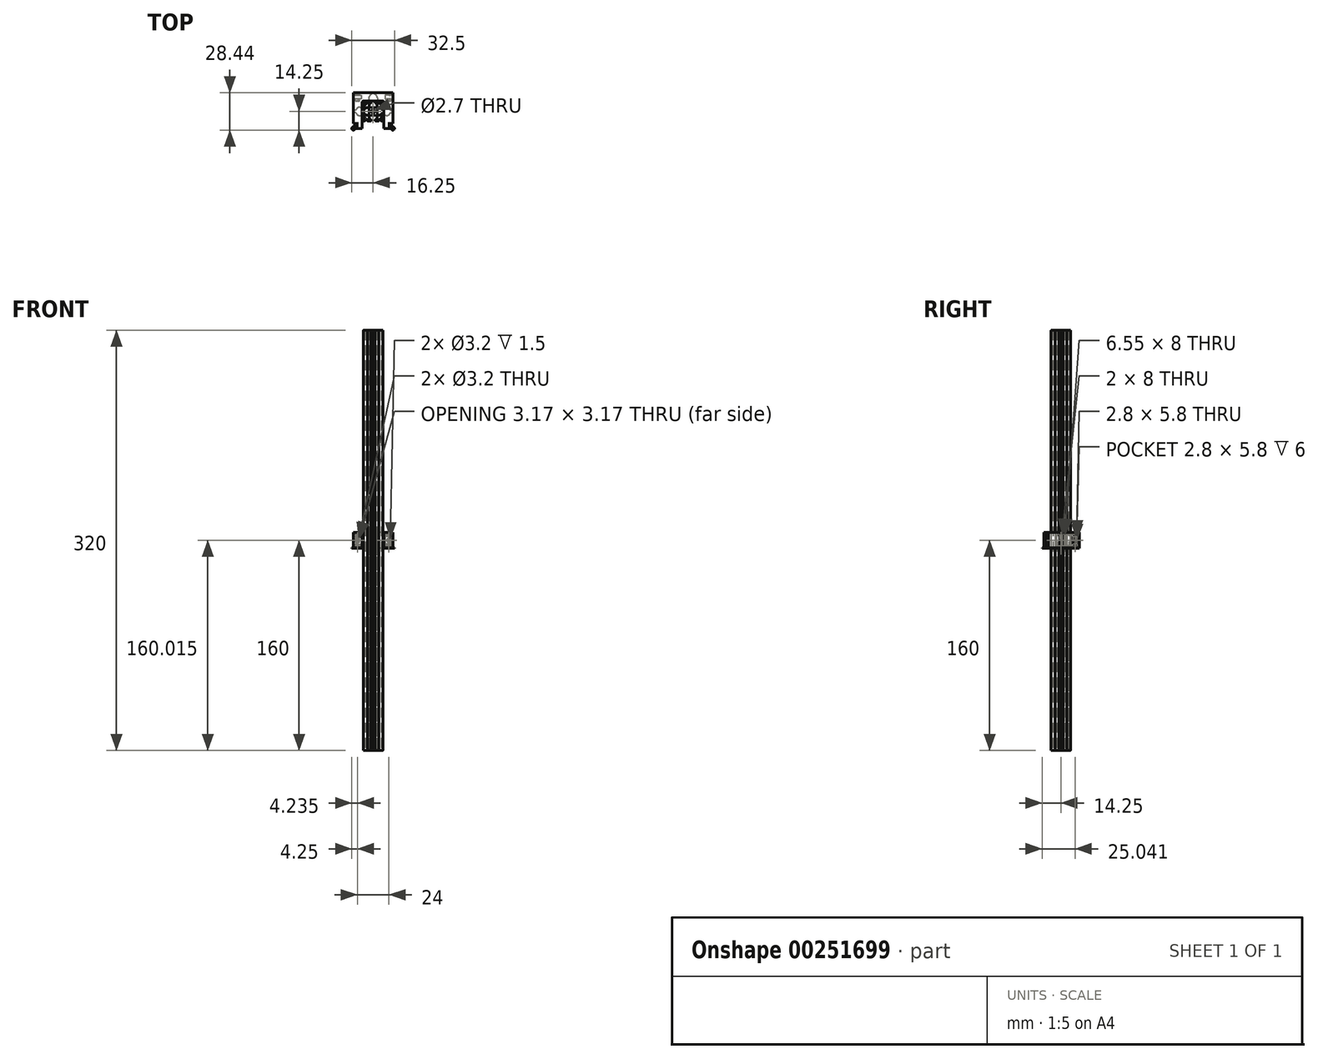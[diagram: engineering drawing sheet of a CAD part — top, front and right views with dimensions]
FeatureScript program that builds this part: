
annotation { "Feature Type Name" : "Feature", "Feature Type Description" : "" }
export const myFeature = defineFeature(function(context is Context, id is Id, definition is map)
    precondition{}
    {
        {
            var Q0;
            Q0=qCreatedBy(makeId("Top.planeOp"),FACE);
            var sketch = newSketch(context, id + "F0", { "sketchPlane" : qUnion([Q0])});
            skLineSegment(sketch, "E0", {"start": v(0, 0) * mm, "end": v(-7.5, -7.5) * mm, "construction": true});
            skArc(sketch, "E1", {"start": v(-1.35, 0) * mm, "mid": v(-1.25, -0.52) * mm, "end": v(-0.95, -0.95) * mm});
            skLineSegment(sketch, "E2", {"start": v(-7.5, -7) * mm, "end": v(-7.5, -6.72) * mm});
            skLineSegment(sketch, "E3", {"start": v(-7.35, -6.36) * mm, "end": v(-6.25, -5.26) * mm});
            skLineSegment(sketch, "E4", {"start": v(-6.6, -4.4) * mm, "end": v(-7, -4.4) * mm});
            skLineSegment(sketch, "E5", {"start": v(-7.5, -3.9) * mm, "end": v(-7.5, -2.1) * mm});
            skLineSegment(sketch, "E6", {"start": v(-7, -1.6) * mm, "end": v(-6.6, -1.6) * mm});
            skLineSegment(sketch, "E7", {"start": v(-6.1, -2.1) * mm, "end": v(-6.1, -2.7) * mm});
            skLineSegment(sketch, "E8", {"start": v(-5.9, -2.9) * mm, "end": v(-3.74, -2.9) * mm});
            skLineSegment(sketch, "E9", {"start": v(-3.25, -2.49) * mm, "end": v(-2.93, -0.73) * mm});
            skLineSegment(sketch, "E10", {"start": v(-2.73, -0.57) * mm, "end": v(-2.6, -0.57) * mm});
            skLineSegment(sketch, "E11", {"start": v(-2.4, -0.37) * mm, "end": v(-2.4, 0) * mm});
            skLineSegment(sketch, "E12", {"start": v(-2.4, 0) * mm, "end": v(-1.35, 0) * mm, "construction": true});
            skPoint(sketch, "E13.visualSharp", {"position": v(-5.4, -4.4) * mm});
            skArc(sketch, "E13.filletArc", {"start": v(-6.25, -5.26) * mm, "mid": v(-6.14, -4.71) * mm, "end": v(-6.6, -4.4) * mm});
            skPoint(sketch, "E14.visualSharp", {"position": v(-6.1, -2.9) * mm});
            skArc(sketch, "E14.filletArc", {"start": v(-6.1, -2.7) * mm, "mid": v(-6.04, -2.84) * mm, "end": v(-5.9, -2.9) * mm});
            skPoint(sketch, "E15.visualSharp", {"position": v(-6.1, -1.6) * mm});
            skArc(sketch, "E15.filletArc", {"start": v(-6.1, -2.1) * mm, "mid": v(-6.25, -1.75) * mm, "end": v(-6.6, -1.6) * mm});
            skPoint(sketch, "E16.visualSharp", {"position": v(-7.5, -1.6) * mm});
            skArc(sketch, "E16.filletArc", {"start": v(-7, -1.6) * mm, "mid": v(-7.35, -1.75) * mm, "end": v(-7.5, -2.1) * mm});
            skPoint(sketch, "E17.visualSharp", {"position": v(-7.5, -4.4) * mm});
            skArc(sketch, "E17.filletArc", {"start": v(-7.5, -3.9) * mm, "mid": v(-7.35, -4.26) * mm, "end": v(-7, -4.4) * mm});
            skPoint(sketch, "E18.visualSharp", {"position": v(-7.5, -6.51) * mm});
            skArc(sketch, "E18.filletArc", {"start": v(-7.35, -6.36) * mm, "mid": v(-7.46, -6.53) * mm, "end": v(-7.5, -6.72) * mm});
            skPoint(sketch, "E19.visualSharp", {"position": v(-3.32, -2.9) * mm});
            skArc(sketch, "E19.filletArc", {"start": v(-3.74, -2.9) * mm, "mid": v(-3.42, -2.78) * mm, "end": v(-3.25, -2.49) * mm});
            skPoint(sketch, "E20.visualSharp", {"position": v(-2.9, -0.57) * mm});
            skArc(sketch, "E20.filletArc", {"start": v(-2.73, -0.57) * mm, "mid": v(-2.86, -0.62) * mm, "end": v(-2.93, -0.73) * mm});
            skPoint(sketch, "E21.visualSharp", {"position": v(-2.4, -0.57) * mm});
            skArc(sketch, "E21.filletArc", {"start": v(-2.6, -0.57) * mm, "mid": v(-2.46, -0.51) * mm, "end": v(-2.4, -0.37) * mm});
            skLineSegment(sketch, "E22.0.MirrorCS", {"start": v(0, -2.4) * mm, "end": v(0, -1.35) * mm, "construction": true});
            skPoint(sketch, "E22.1.MirrorP", {"position": v(-4.4, -7.5) * mm});
            skArc(sketch, "E22.2.MirrorCS", {"start": v(-6.36, -7.35) * mm, "mid": v(-6.53, -7.46) * mm, "end": v(-6.72, -7.5) * mm});
            skPoint(sketch, "E22.3.MirrorP", {"position": v(-1.6, -7.5) * mm});
            skArc(sketch, "E22.4.MirrorCS", {"start": v(-1.6, -7) * mm, "mid": v(-1.75, -7.35) * mm, "end": v(-2.1, -7.5) * mm});
            skArc(sketch, "E22.5.MirrorCS", {"start": v(-0.57, -2.73) * mm, "mid": v(-0.62, -2.86) * mm, "end": v(-0.73, -2.93) * mm});
            skPoint(sketch, "E22.6.MirrorP", {"position": v(-1.6, -6.1) * mm});
            skLineSegment(sketch, "E22.7.MirrorCS", {"start": v(-3.9, -7.5) * mm, "end": v(-2.1, -7.5) * mm});
            skArc(sketch, "E22.8.MirrorCS", {"start": v(-5.26, -6.25) * mm, "mid": v(-4.71, -6.14) * mm, "end": v(-4.4, -6.6) * mm});
            skPoint(sketch, "E22.9.MirrorP", {"position": v(-0.57, -2.4) * mm});
            skPoint(sketch, "E22.10.MirrorP", {"position": v(-4.4, -5.4) * mm});
            skArc(sketch, "E22.11.MirrorCS", {"start": v(-2.7, -6.1) * mm, "mid": v(-2.84, -6.04) * mm, "end": v(-2.9, -5.9) * mm});
            skPoint(sketch, "E22.12.MirrorP", {"position": v(-0.57, -2.9) * mm});
            skLineSegment(sketch, "E22.13.MirrorCS", {"start": v(-7, -7.5) * mm, "end": v(-6.72, -7.5) * mm});
            skLineSegment(sketch, "E22.14.MirrorCS", {"start": v(-1.6, -7) * mm, "end": v(-1.6, -6.6) * mm});
            skLineSegment(sketch, "E22.15.MirrorCS", {"start": v(-6.36, -7.35) * mm, "end": v(-5.26, -6.25) * mm});
            skArc(sketch, "E22.16.MirrorCS", {"start": v(-2.1, -6.1) * mm, "mid": v(-1.75, -6.25) * mm, "end": v(-1.6, -6.6) * mm});
            skLineSegment(sketch, "E22.17.MirrorCS", {"start": v(-4.4, -6.6) * mm, "end": v(-4.4, -7) * mm});
            skArc(sketch, "E22.18.MirrorCS", {"start": v(-2.9, -3.74) * mm, "mid": v(-2.78, -3.42) * mm, "end": v(-2.49, -3.25) * mm});
            skLineSegment(sketch, "E22.19.MirrorCS", {"start": v(-2.9, -5.9) * mm, "end": v(-2.9, -3.74) * mm});
            skLineSegment(sketch, "E22.20.MirrorCS", {"start": v(-2.1, -6.1) * mm, "end": v(-2.7, -6.1) * mm});
            skArc(sketch, "E22.21.MirrorCS", {"start": v(-0.57, -2.6) * mm, "mid": v(-0.51, -2.46) * mm, "end": v(-0.37, -2.4) * mm});
            skLineSegment(sketch, "E22.22.MirrorCS", {"start": v(-0.37, -2.4) * mm, "end": v(0, -2.4) * mm});
            skPoint(sketch, "E22.23.MirrorP", {"position": v(-6.51, -7.5) * mm});
            skPoint(sketch, "E22.24.MirrorP", {"position": v(-2.9, -6.1) * mm});
            skLineSegment(sketch, "E22.25.MirrorCS", {"start": v(-2.49, -3.25) * mm, "end": v(-0.73, -2.93) * mm});
            skLineSegment(sketch, "E22.26.MirrorCS", {"start": v(-0.57, -2.73) * mm, "end": v(-0.57, -2.6) * mm});
            skArc(sketch, "E22.27.MirrorCS", {"start": v(0, -1.35) * mm, "mid": v(-0.52, -1.25) * mm, "end": v(-0.95, -0.95) * mm});
            skArc(sketch, "E22.28.MirrorCS", {"start": v(-3.9, -7.5) * mm, "mid": v(-4.26, -7.35) * mm, "end": v(-4.4, -7) * mm});
            skPoint(sketch, "E22.29.MirrorP", {"position": v(-2.9, -3.32) * mm});
            skPoint(sketch, "E23.visualSharp", {"position": v(-7.5, -7.5) * mm});
            skArc(sketch, "E23.filletArc", {"start": v(-7.5, -7) * mm, "mid": v(-7.35, -7.35) * mm, "end": v(-7, -7.5) * mm});
            skLineSegment(sketch, "E24.0.MirrorCS", {"start": v(0, 2.4) * mm, "end": v(0, 1.35) * mm, "construction": true});
            skLineSegment(sketch, "E24.1.MirrorCS", {"start": v(-2.1, 6.1) * mm, "end": v(-2.7, 6.1) * mm});
            skLineSegment(sketch, "E24.2.MirrorCS", {"start": v(-7.5, 3.9) * mm, "end": v(-7.5, 2.1) * mm});
            skLineSegment(sketch, "E24.3.MirrorCS", {"start": v(-7, 1.6) * mm, "end": v(-6.6, 1.6) * mm});
            skArc(sketch, "E24.4.MirrorCS", {"start": v(-6.1, 2.1) * mm, "mid": v(-6.25, 1.75) * mm, "end": v(-6.6, 1.6) * mm});
            skPoint(sketch, "E24.5.MirrorP", {"position": v(-3.32, 2.9) * mm});
            skPoint(sketch, "E24.6.MirrorP", {"position": v(-0.57, 2.9) * mm});
            skArc(sketch, "E24.7.MirrorCS", {"start": v(-0.57, 2.6) * mm, "mid": v(-0.51, 2.46) * mm, "end": v(-0.37, 2.4) * mm});
            skArc(sketch, "E24.8.MirrorCS", {"start": v(-2.6, 0.57) * mm, "mid": v(-2.46, 0.51) * mm, "end": v(-2.4, 0.37) * mm});
            skLineSegment(sketch, "E24.9.MirrorCS", {"start": v(-0.37, 2.4) * mm, "end": v(0, 2.4) * mm});
            skArc(sketch, "E24.10.MirrorCS", {"start": v(-6.1, 2.7) * mm, "mid": v(-6.04, 2.84) * mm, "end": v(-5.9, 2.9) * mm});
            skPoint(sketch, "E24.11.MirrorP", {"position": v(-4.4, 5.4) * mm});
            skLineSegment(sketch, "E24.12.MirrorCS", {"start": v(-2.9, 5.9) * mm, "end": v(-2.9, 3.74) * mm});
            skLineSegment(sketch, "E24.13.MirrorCS", {"start": v(-7.35, 6.36) * mm, "end": v(-6.25, 5.26) * mm});
            skPoint(sketch, "E24.14.MirrorP", {"position": v(-7.5, 6.51) * mm});
            skArc(sketch, "E24.15.MirrorCS", {"start": v(-3.74, 2.9) * mm, "mid": v(-3.42, 2.78) * mm, "end": v(-3.25, 2.49) * mm});
            skArc(sketch, "E24.16.MirrorCS", {"start": v(-2.1, 6.1) * mm, "mid": v(-1.75, 6.25) * mm, "end": v(-1.6, 6.6) * mm});
            skArc(sketch, "E24.17.MirrorCS", {"start": v(-7, 1.6) * mm, "mid": v(-7.35, 1.75) * mm, "end": v(-7.5, 2.1) * mm});
            skPoint(sketch, "E24.18.MirrorP", {"position": v(-1.6, 6.1) * mm});
            skPoint(sketch, "E24.19.MirrorP", {"position": v(-7.5, 4.4) * mm});
            skLineSegment(sketch, "E24.20.MirrorCS", {"start": v(-4.4, 6.6) * mm, "end": v(-4.4, 7) * mm});
            skArc(sketch, "E24.21.MirrorCS", {"start": v(-7.5, 3.9) * mm, "mid": v(-7.35, 4.26) * mm, "end": v(-7, 4.4) * mm});
            skPoint(sketch, "E24.22.MirrorP", {"position": v(-0.57, 2.4) * mm});
            skLineSegment(sketch, "E24.23.MirrorCS", {"start": v(-5.9, 2.9) * mm, "end": v(-3.74, 2.9) * mm});
            skArc(sketch, "E24.24.MirrorCS", {"start": v(-2.9, 3.74) * mm, "mid": v(-2.78, 3.42) * mm, "end": v(-2.49, 3.25) * mm});
            skArc(sketch, "E24.25.MirrorCS", {"start": v(-7.35, 6.36) * mm, "mid": v(-7.46, 6.53) * mm, "end": v(-7.5, 6.72) * mm});
            skPoint(sketch, "E24.26.MirrorP", {"position": v(-6.1, 2.9) * mm});
            skPoint(sketch, "E24.27.MirrorP", {"position": v(-4.4, 7.5) * mm});
            skArc(sketch, "E24.28.MirrorCS", {"start": v(-5.26, 6.25) * mm, "mid": v(-4.71, 6.14) * mm, "end": v(-4.4, 6.6) * mm});
            skArc(sketch, "E24.29.MirrorCS", {"start": v(-7.5, 7) * mm, "mid": v(-7.35, 7.35) * mm, "end": v(-7, 7.5) * mm});
            skPoint(sketch, "E24.30.MirrorP", {"position": v(-6.1, 1.6) * mm});
            skPoint(sketch, "E24.31.MirrorP", {"position": v(-2.9, 3.32) * mm});
            skPoint(sketch, "E24.32.MirrorP", {"position": v(-1.6, 7.5) * mm});
            skPoint(sketch, "E24.33.MirrorP", {"position": v(-2.9, 6.1) * mm});
            skLineSegment(sketch, "E24.34.MirrorCS", {"start": v(-3.9, 7.5) * mm, "end": v(-2.1, 7.5) * mm});
            skLineSegment(sketch, "E24.35.MirrorCS", {"start": v(-7, 7.5) * mm, "end": v(-6.72, 7.5) * mm});
            skArc(sketch, "E24.36.MirrorCS", {"start": v(-3.9, 7.5) * mm, "mid": v(-4.26, 7.35) * mm, "end": v(-4.4, 7) * mm});
            skPoint(sketch, "E24.37.MirrorP", {"position": v(-7.5, 7.5) * mm});
            skLineSegment(sketch, "E24.38.MirrorCS", {"start": v(-1.6, 7) * mm, "end": v(-1.6, 6.6) * mm});
            skLineSegment(sketch, "E24.39.MirrorCS", {"start": v(-6.36, 7.35) * mm, "end": v(-5.26, 6.25) * mm});
            skPoint(sketch, "E24.40.MirrorP", {"position": v(-7.5, 1.6) * mm});
            skArc(sketch, "E24.41.MirrorCS", {"start": v(-2.7, 6.1) * mm, "mid": v(-2.84, 6.04) * mm, "end": v(-2.9, 5.9) * mm});
            skArc(sketch, "E24.42.MirrorCS", {"start": v(-6.36, 7.35) * mm, "mid": v(-6.53, 7.46) * mm, "end": v(-6.72, 7.5) * mm});
            skLineSegment(sketch, "E24.43.MirrorCS", {"start": v(-2.49, 3.25) * mm, "end": v(-0.73, 2.93) * mm});
            skPoint(sketch, "E24.44.MirrorP", {"position": v(-2.9, 0.57) * mm});
            skLineSegment(sketch, "E24.45.MirrorCS", {"start": v(-6.6, 4.4) * mm, "end": v(-7, 4.4) * mm});
            skArc(sketch, "E24.46.MirrorCS", {"start": v(-1.6, 7) * mm, "mid": v(-1.75, 7.35) * mm, "end": v(-2.1, 7.5) * mm});
            skArc(sketch, "E24.47.MirrorCS", {"start": v(-2.73, 0.57) * mm, "mid": v(-2.86, 0.62) * mm, "end": v(-2.93, 0.73) * mm});
            skArc(sketch, "E24.48.MirrorCS", {"start": v(-6.25, 5.26) * mm, "mid": v(-6.14, 4.71) * mm, "end": v(-6.6, 4.4) * mm});
            skLineSegment(sketch, "E24.49.MirrorCS", {"start": v(-0.57, 2.73) * mm, "end": v(-0.57, 2.6) * mm});
            skLineSegment(sketch, "E24.50.MirrorCS", {"start": v(-2.73, 0.57) * mm, "end": v(-2.6, 0.57) * mm});
            skArc(sketch, "E24.51.MirrorCS", {"start": v(-1.35, 0) * mm, "mid": v(-1.25, 0.52) * mm, "end": v(-0.95, 0.95) * mm});
            skPoint(sketch, "E24.52.MirrorP", {"position": v(-2.4, 0.57) * mm});
            skPoint(sketch, "E24.53.MirrorP", {"position": v(-5.4, 4.4) * mm});
            skLineSegment(sketch, "E24.54.MirrorCS", {"start": v(-2.4, 0.37) * mm, "end": v(-2.4, 0) * mm});
            skArc(sketch, "E24.55.MirrorCS", {"start": v(0, 1.35) * mm, "mid": v(-0.52, 1.25) * mm, "end": v(-0.95, 0.95) * mm});
            skLineSegment(sketch, "E24.56.MirrorCS", {"start": v(-3.25, 2.49) * mm, "end": v(-2.93, 0.73) * mm});
            skLineSegment(sketch, "E24.57.MirrorCS", {"start": v(-6.1, 2.1) * mm, "end": v(-6.1, 2.7) * mm});
            skLineSegment(sketch, "E24.58.MirrorCS", {"start": v(-7.5, 7) * mm, "end": v(-7.5, 6.72) * mm});
            skArc(sketch, "E24.59.MirrorCS", {"start": v(-0.57, 2.73) * mm, "mid": v(-0.62, 2.86) * mm, "end": v(-0.73, 2.93) * mm});
            skPoint(sketch, "E24.60.MirrorP", {"position": v(-6.51, 7.5) * mm});
            skLineSegment(sketch, "E25.0.MirrorCS", {"start": v(7, -7.5) * mm, "end": v(6.72, -7.5) * mm});
            skLineSegment(sketch, "E25.1.MirrorCS", {"start": v(0.57, 2.73) * mm, "end": v(0.57, 2.6) * mm});
            skLineSegment(sketch, "E25.2.MirrorCS", {"start": v(0.37, 2.4) * mm, "end": v(0, 2.4) * mm});
            skLineSegment(sketch, "E25.3.MirrorCS", {"start": v(7, 7.5) * mm, "end": v(6.72, 7.5) * mm});
            skLineSegment(sketch, "E25.4.MirrorCS", {"start": v(1.6, -7) * mm, "end": v(1.6, -6.6) * mm});
            skLineSegment(sketch, "E25.5.MirrorCS", {"start": v(2.73, 0.57) * mm, "end": v(2.6, 0.57) * mm});
            skLineSegment(sketch, "E25.6.MirrorCS", {"start": v(7, 1.6) * mm, "end": v(6.6, 1.6) * mm});
            skLineSegment(sketch, "E25.7.MirrorCS", {"start": v(5.9, 2.9) * mm, "end": v(3.74, 2.9) * mm});
            skLineSegment(sketch, "E25.8.MirrorCS", {"start": v(7.35, 6.36) * mm, "end": v(6.25, 5.26) * mm});
            skArc(sketch, "E25.9.MirrorCS", {"start": v(2.7, -6.1) * mm, "mid": v(2.84, -6.04) * mm, "end": v(2.9, -5.9) * mm});
            skArc(sketch, "E25.10.MirrorCS", {"start": v(2.9, 3.74) * mm, "mid": v(2.78, 3.42) * mm, "end": v(2.49, 3.25) * mm});
            skPoint(sketch, "E25.11.MirrorP", {"position": v(1.6, -7.5) * mm});
            skPoint(sketch, "E25.12.MirrorP", {"position": v(6.1, -1.6) * mm});
            skPoint(sketch, "E25.13.MirrorP", {"position": v(2.9, 3.32) * mm});
            skPoint(sketch, "E25.14.MirrorP", {"position": v(7.5, -1.6) * mm});
            skArc(sketch, "E25.15.MirrorCS", {"start": v(1.6, 7) * mm, "mid": v(1.75, 7.35) * mm, "end": v(2.1, 7.5) * mm});
            skLineSegment(sketch, "E25.16.MirrorCS", {"start": v(6.1, -2.1) * mm, "end": v(6.1, -2.7) * mm});
            skLineSegment(sketch, "E25.17.MirrorCS", {"start": v(2.4, 0.37) * mm, "end": v(2.4, 0) * mm});
            skArc(sketch, "E25.18.MirrorCS", {"start": v(7, -1.6) * mm, "mid": v(7.35, -1.75) * mm, "end": v(7.5, -2.1) * mm});
            skArc(sketch, "E25.19.MirrorCS", {"start": v(7.5, 7) * mm, "mid": v(7.35, 7.35) * mm, "end": v(7, 7.5) * mm});
            skArc(sketch, "E25.20.MirrorCS", {"start": v(2.1, -6.1) * mm, "mid": v(1.75, -6.25) * mm, "end": v(1.6, -6.6) * mm});
            skArc(sketch, "E25.21.MirrorCS", {"start": v(6.1, 2.1) * mm, "mid": v(6.25, 1.75) * mm, "end": v(6.6, 1.6) * mm});
            skLineSegment(sketch, "E25.22.MirrorCS", {"start": v(4.4, 6.6) * mm, "end": v(4.4, 7) * mm});
            skLineSegment(sketch, "E25.23.MirrorCS", {"start": v(6.6, 4.4) * mm, "end": v(7, 4.4) * mm});
            skArc(sketch, "E25.24.MirrorCS", {"start": v(7, 1.6) * mm, "mid": v(7.35, 1.75) * mm, "end": v(7.5, 2.1) * mm});
            skArc(sketch, "E25.25.MirrorCS", {"start": v(0, -1.35) * mm, "mid": v(0.52, -1.25) * mm, "end": v(0.95, -0.95) * mm});
            skLineSegment(sketch, "E25.26.MirrorCS", {"start": v(3.9, -7.5) * mm, "end": v(2.1, -7.5) * mm});
            skLineSegment(sketch, "E25.27.MirrorCS", {"start": v(2.1, 6.1) * mm, "end": v(2.7, 6.1) * mm});
            skLineSegment(sketch, "E25.28.MirrorCS", {"start": v(2.73, -0.57) * mm, "end": v(2.6, -0.57) * mm});
            skLineSegment(sketch, "E25.29.MirrorCS", {"start": v(4.4, -6.6) * mm, "end": v(4.4, -7) * mm});
            skLineSegment(sketch, "E25.30.MirrorCS", {"start": v(3.9, 7.5) * mm, "end": v(2.1, 7.5) * mm});
            skArc(sketch, "E25.31.MirrorCS", {"start": v(0.57, -2.73) * mm, "mid": v(0.62, -2.86) * mm, "end": v(0.73, -2.93) * mm});
            skArc(sketch, "E25.32.MirrorCS", {"start": v(0.57, 2.6) * mm, "mid": v(0.51, 2.46) * mm, "end": v(0.37, 2.4) * mm});
            skPoint(sketch, "E25.33.MirrorP", {"position": v(6.51, -7.5) * mm});
            skArc(sketch, "E25.34.MirrorCS", {"start": v(3.9, -7.5) * mm, "mid": v(4.26, -7.35) * mm, "end": v(4.4, -7) * mm});
            skArc(sketch, "E25.35.MirrorCS", {"start": v(2.7, 6.1) * mm, "mid": v(2.84, 6.04) * mm, "end": v(2.9, 5.9) * mm});
            skPoint(sketch, "E25.36.MirrorP", {"position": v(0.57, -2.4) * mm});
            skPoint(sketch, "E25.37.MirrorP", {"position": v(0.57, 2.9) * mm});
            skLineSegment(sketch, "E25.38.MirrorCS", {"start": v(3.25, -2.49) * mm, "end": v(2.93, -0.73) * mm});
            skPoint(sketch, "E25.39.MirrorP", {"position": v(5.4, -4.4) * mm});
            skPoint(sketch, "E25.40.MirrorP", {"position": v(2.4, -0.57) * mm});
            skLineSegment(sketch, "E25.41.MirrorCS", {"start": v(7.5, -7) * mm, "end": v(7.5, -6.72) * mm});
            skArc(sketch, "E25.42.MirrorCS", {"start": v(7.35, 6.36) * mm, "mid": v(7.46, 6.53) * mm, "end": v(7.5, 6.72) * mm});
            skPoint(sketch, "E25.43.MirrorP", {"position": v(4.4, 7.5) * mm});
            skArc(sketch, "E25.44.MirrorCS", {"start": v(6.25, 5.26) * mm, "mid": v(6.14, 4.71) * mm, "end": v(6.6, 4.4) * mm});
            skPoint(sketch, "E25.45.MirrorP", {"position": v(6.1, -2.9) * mm});
            skPoint(sketch, "E25.46.MirrorP", {"position": v(4.4, -7.5) * mm});
            skArc(sketch, "E25.47.MirrorCS", {"start": v(6.1, 2.7) * mm, "mid": v(6.04, 2.84) * mm, "end": v(5.9, 2.9) * mm});
            skLineSegment(sketch, "E25.48.MirrorCS", {"start": v(2.1, -6.1) * mm, "end": v(2.7, -6.1) * mm});
            skArc(sketch, "E25.49.MirrorCS", {"start": v(2.73, -0.57) * mm, "mid": v(2.86, -0.62) * mm, "end": v(2.93, -0.73) * mm});
            skArc(sketch, "E25.50.MirrorCS", {"start": v(7.35, -6.36) * mm, "mid": v(7.46, -6.53) * mm, "end": v(7.5, -6.72) * mm});
            skLineSegment(sketch, "E25.51.MirrorCS", {"start": v(3.25, 2.49) * mm, "end": v(2.93, 0.73) * mm});
            skArc(sketch, "E25.52.MirrorCS", {"start": v(2.9, -3.74) * mm, "mid": v(2.78, -3.42) * mm, "end": v(2.49, -3.25) * mm});
            skArc(sketch, "E25.53.MirrorCS", {"start": v(2.6, 0.57) * mm, "mid": v(2.46, 0.51) * mm, "end": v(2.4, 0.37) * mm});
            skPoint(sketch, "E25.54.MirrorP", {"position": v(2.9, 0.57) * mm});
            skPoint(sketch, "E25.55.MirrorP", {"position": v(7.5, -6.51) * mm});
            skLineSegment(sketch, "E25.56.MirrorCS", {"start": v(2.49, 3.25) * mm, "end": v(0.73, 2.93) * mm});
            skArc(sketch, "E25.57.MirrorCS", {"start": v(1.6, -7) * mm, "mid": v(1.75, -7.35) * mm, "end": v(2.1, -7.5) * mm});
            skArc(sketch, "E25.58.MirrorCS", {"start": v(2.1, 6.1) * mm, "mid": v(1.75, 6.25) * mm, "end": v(1.6, 6.6) * mm});
            skLineSegment(sketch, "E25.59.MirrorCS", {"start": v(0.57, -2.73) * mm, "end": v(0.57, -2.6) * mm});
            skLineSegment(sketch, "E25.60.MirrorCS", {"start": v(2.4, -0.37) * mm, "end": v(2.4, 0) * mm});
            skArc(sketch, "E25.61.MirrorCS", {"start": v(7.5, -3.9) * mm, "mid": v(7.35, -4.26) * mm, "end": v(7, -4.4) * mm});
            skLineSegment(sketch, "E25.62.MirrorCS", {"start": v(5.9, -2.9) * mm, "end": v(3.74, -2.9) * mm});
            skLineSegment(sketch, "E25.63.MirrorCS", {"start": v(7.5, -3.9) * mm, "end": v(7.5, -2.1) * mm});
            skLineSegment(sketch, "E25.64.MirrorCS", {"start": v(7, -1.6) * mm, "end": v(6.6, -1.6) * mm});
            skArc(sketch, "E25.65.MirrorCS", {"start": v(1.35, 0) * mm, "mid": v(1.25, -0.52) * mm, "end": v(0.95, -0.95) * mm});
            skPoint(sketch, "E25.66.MirrorP", {"position": v(7.5, 1.6) * mm});
            skPoint(sketch, "E25.67.MirrorP", {"position": v(1.6, 6.1) * mm});
            skLineSegment(sketch, "E25.68.MirrorCS", {"start": v(6.36, -7.35) * mm, "end": v(5.26, -6.25) * mm});
            skPoint(sketch, "E25.69.MirrorP", {"position": v(2.4, 0.57) * mm});
            skPoint(sketch, "E25.70.MirrorP", {"position": v(6.1, 1.6) * mm});
            skPoint(sketch, "E25.71.MirrorP", {"position": v(3.32, -2.9) * mm});
            skPoint(sketch, "E25.72.MirrorP", {"position": v(0.57, -2.9) * mm});
            skPoint(sketch, "E25.73.MirrorP", {"position": v(7.5, 4.4) * mm});
            skArc(sketch, "E25.74.MirrorCS", {"start": v(5.26, -6.25) * mm, "mid": v(4.71, -6.14) * mm, "end": v(4.4, -6.6) * mm});
            skArc(sketch, "E25.75.MirrorCS", {"start": v(7.5, -7) * mm, "mid": v(7.35, -7.35) * mm, "end": v(7, -7.5) * mm});
            skLineSegment(sketch, "E25.76.MirrorCS", {"start": v(2.49, -3.25) * mm, "end": v(0.73, -2.93) * mm});
            skArc(sketch, "E25.77.MirrorCS", {"start": v(3.74, 2.9) * mm, "mid": v(3.42, 2.78) * mm, "end": v(3.25, 2.49) * mm});
            skArc(sketch, "E25.78.MirrorCS", {"start": v(6.36, -7.35) * mm, "mid": v(6.53, -7.46) * mm, "end": v(6.72, -7.5) * mm});
            skArc(sketch, "E25.79.MirrorCS", {"start": v(7.5, 3.9) * mm, "mid": v(7.35, 4.26) * mm, "end": v(7, 4.4) * mm});
            skArc(sketch, "E25.80.MirrorCS", {"start": v(2.73, 0.57) * mm, "mid": v(2.86, 0.62) * mm, "end": v(2.93, 0.73) * mm});
            skArc(sketch, "E25.81.MirrorCS", {"start": v(6.36, 7.35) * mm, "mid": v(6.53, 7.46) * mm, "end": v(6.72, 7.5) * mm});
            skPoint(sketch, "E25.82.MirrorP", {"position": v(4.4, -5.4) * mm});
            skPoint(sketch, "E25.83.MirrorP", {"position": v(6.51, 7.5) * mm});
            skPoint(sketch, "E25.84.MirrorP", {"position": v(2.9, -0.57) * mm});
            skLineSegment(sketch, "E25.85.MirrorCS", {"start": v(2.9, -5.9) * mm, "end": v(2.9, -3.74) * mm});
            skLineSegment(sketch, "E25.86.MirrorCS", {"start": v(6.1, 2.1) * mm, "end": v(6.1, 2.7) * mm});
            skLineSegment(sketch, "E25.87.MirrorCS", {"start": v(6.36, 7.35) * mm, "end": v(5.26, 6.25) * mm});
            skArc(sketch, "E25.88.MirrorCS", {"start": v(0.57, 2.73) * mm, "mid": v(0.62, 2.86) * mm, "end": v(0.73, 2.93) * mm});
            skArc(sketch, "E25.89.MirrorCS", {"start": v(0.57, -2.6) * mm, "mid": v(0.51, -2.46) * mm, "end": v(0.37, -2.4) * mm});
            skLineSegment(sketch, "E25.90.MirrorCS", {"start": v(2.9, 5.9) * mm, "end": v(2.9, 3.74) * mm});
            skArc(sketch, "E25.91.MirrorCS", {"start": v(0, 1.35) * mm, "mid": v(0.52, 1.25) * mm, "end": v(0.95, 0.95) * mm});
            skArc(sketch, "E25.92.MirrorCS", {"start": v(2.6, -0.57) * mm, "mid": v(2.46, -0.51) * mm, "end": v(2.4, -0.37) * mm});
            skPoint(sketch, "E25.93.MirrorP", {"position": v(4.4, 5.4) * mm});
            skPoint(sketch, "E25.94.MirrorP", {"position": v(2.9, -3.32) * mm});
            skPoint(sketch, "E25.95.MirrorP", {"position": v(2.9, 6.1) * mm});
            skPoint(sketch, "E25.96.MirrorP", {"position": v(5.4, 4.4) * mm});
            skPoint(sketch, "E25.97.MirrorP", {"position": v(3.32, 2.9) * mm});
            skArc(sketch, "E25.98.MirrorCS", {"start": v(3.74, -2.9) * mm, "mid": v(3.42, -2.78) * mm, "end": v(3.25, -2.49) * mm});
            skArc(sketch, "E25.99.MirrorCS", {"start": v(3.9, 7.5) * mm, "mid": v(4.26, 7.35) * mm, "end": v(4.4, 7) * mm});
            skPoint(sketch, "E25.100.MirrorP", {"position": v(7.5, -4.4) * mm});
            skPoint(sketch, "E25.101.MirrorP", {"position": v(6.1, 2.9) * mm});
            skArc(sketch, "E25.102.MirrorCS", {"start": v(1.35, 0) * mm, "mid": v(1.25, 0.52) * mm, "end": v(0.95, 0.95) * mm});
            skArc(sketch, "E25.103.MirrorCS", {"start": v(5.26, 6.25) * mm, "mid": v(4.71, 6.14) * mm, "end": v(4.4, 6.6) * mm});
            skPoint(sketch, "E25.104.MirrorP", {"position": v(7.5, 6.51) * mm});
            skPoint(sketch, "E25.105.MirrorP", {"position": v(2.9, -6.1) * mm});
            skArc(sketch, "E25.106.MirrorCS", {"start": v(6.25, -5.26) * mm, "mid": v(6.14, -4.71) * mm, "end": v(6.6, -4.4) * mm});
            skArc(sketch, "E25.107.MirrorCS", {"start": v(6.1, -2.1) * mm, "mid": v(6.25, -1.75) * mm, "end": v(6.6, -1.6) * mm});
            skPoint(sketch, "E25.108.MirrorP", {"position": v(1.6, 7.5) * mm});
            skPoint(sketch, "E25.109.MirrorP", {"position": v(7.5, 7.5) * mm});
            skLineSegment(sketch, "E25.110.MirrorCS", {"start": v(0.37, -2.4) * mm, "end": v(0, -2.4) * mm});
            skPoint(sketch, "E25.111.MirrorP", {"position": v(7.5, -7.5) * mm});
            skLineSegment(sketch, "E25.112.MirrorCS", {"start": v(7.5, 7) * mm, "end": v(7.5, 6.72) * mm});
            skArc(sketch, "E25.113.MirrorCS", {"start": v(6.1, -2.7) * mm, "mid": v(6.04, -2.84) * mm, "end": v(5.9, -2.9) * mm});
            skLineSegment(sketch, "E25.114.MirrorCS", {"start": v(1.6, 7) * mm, "end": v(1.6, 6.6) * mm});
            skPoint(sketch, "E25.115.MirrorP", {"position": v(1.6, -6.1) * mm});
            skLineSegment(sketch, "E25.116.MirrorCS", {"start": v(7.35, -6.36) * mm, "end": v(6.25, -5.26) * mm});
            skLineSegment(sketch, "E25.117.MirrorCS", {"start": v(7.5, 3.9) * mm, "end": v(7.5, 2.1) * mm});
            skPoint(sketch, "E25.118.MirrorP", {"position": v(0.57, 2.4) * mm});
            skLineSegment(sketch, "E25.119.MirrorCS", {"start": v(6.6, -4.4) * mm, "end": v(7, -4.4) * mm});
            skSolve(sketch);
        }
        {
            var Q0;
            Q0=qCreatedBy(makeId("Top.planeOp"),FACE);
            var sketch = newSketch(context, id + "F1", { "sketchPlane" : qUnion([Q0])});
            skLineSegment(sketch, "E26.0", {"start": v(6.36, -7.35) * mm, "end": v(5.26, -6.25) * mm, "construction": true});
            skLineSegment(sketch, "E26.1", {"start": v(-3.25, -2.49) * mm, "end": v(-2.93, -0.73) * mm, "construction": true});
            skArc(sketch, "E26.2", {"start": v(5.26, 6.25) * mm, "mid": v(4.71, 6.14) * mm, "end": v(4.4, 6.6) * mm, "construction": true});
            skLineSegment(sketch, "E26.3", {"start": v(7.5, -3.9) * mm, "end": v(7.5, -2.1) * mm, "construction": true});
            skArc(sketch, "E26.4", {"start": v(6.25, 5.26) * mm, "mid": v(6.14, 4.71) * mm, "end": v(6.6, 4.4) * mm, "construction": true});
            skLineSegment(sketch, "E26.5", {"start": v(-5.9, 2.9) * mm, "end": v(-3.74, 2.9) * mm, "construction": true});
            skLineSegment(sketch, "E26.6", {"start": v(-2.9, 5.9) * mm, "end": v(-2.9, 3.74) * mm, "construction": true});
            skArc(sketch, "E26.7", {"start": v(0, 1.35) * mm, "mid": v(-0.52, 1.25) * mm, "end": v(-0.95, 0.95) * mm, "construction": true});
            skLineSegment(sketch, "E26.8", {"start": v(2.9, 5.9) * mm, "end": v(2.9, 3.74) * mm, "construction": true});
            skLineSegment(sketch, "E26.9", {"start": v(-2.49, -3.25) * mm, "end": v(-0.73, -2.93) * mm, "construction": true});
            skLineSegment(sketch, "E26.10", {"start": v(-7.5, -3.9) * mm, "end": v(-7.5, -2.1) * mm, "construction": true});
            skLineSegment(sketch, "E26.11", {"start": v(3.25, 2.49) * mm, "end": v(2.93, 0.73) * mm, "construction": true});
            skLineSegment(sketch, "E26.12", {"start": v(2.49, -3.25) * mm, "end": v(0.73, -2.93) * mm, "construction": true});
            skLineSegment(sketch, "E26.13", {"start": v(-3.9, 7.5) * mm, "end": v(-2.1, 7.5) * mm, "construction": true});
            skLineSegment(sketch, "E26.14", {"start": v(5.9, 2.9) * mm, "end": v(3.74, 2.9) * mm, "construction": true});
            skLineSegment(sketch, "E26.15", {"start": v(3.9, 7.5) * mm, "end": v(2.1, 7.5) * mm, "construction": true});
            skLineSegment(sketch, "E26.16", {"start": v(-3.9, -7.5) * mm, "end": v(-2.1, -7.5) * mm, "construction": true});
            skLineSegment(sketch, "E26.17", {"start": v(6.36, 7.35) * mm, "end": v(5.26, 6.25) * mm, "construction": true});
            skLineSegment(sketch, "E26.18", {"start": v(-7.5, 3.9) * mm, "end": v(-7.5, 2.1) * mm, "construction": true});
            skLineSegment(sketch, "E26.19", {"start": v(-2.49, 3.25) * mm, "end": v(-0.73, 2.93) * mm, "construction": true});
            skArc(sketch, "E26.20", {"start": v(-6.25, -5.26) * mm, "mid": v(-6.14, -4.71) * mm, "end": v(-6.6, -4.4) * mm, "construction": true});
            skLineSegment(sketch, "E26.21", {"start": v(-7.35, 6.36) * mm, "end": v(-6.25, 5.26) * mm, "construction": true});
            skLineSegment(sketch, "E26.22", {"start": v(5.9, -2.9) * mm, "end": v(3.74, -2.9) * mm, "construction": true});
            skArc(sketch, "E26.23", {"start": v(0, -1.35) * mm, "mid": v(-0.52, -1.25) * mm, "end": v(-0.95, -0.95) * mm, "construction": true});
            skLineSegment(sketch, "E26.24", {"start": v(-3.25, 2.49) * mm, "end": v(-2.93, 0.73) * mm, "construction": true});
            skArc(sketch, "E26.25", {"start": v(0, 1.35) * mm, "mid": v(0.52, 1.25) * mm, "end": v(0.95, 0.95) * mm, "construction": true});
            skArc(sketch, "E26.26", {"start": v(5.26, -6.25) * mm, "mid": v(4.71, -6.14) * mm, "end": v(4.4, -6.6) * mm, "construction": true});
            skLineSegment(sketch, "E26.27", {"start": v(-6.36, 7.35) * mm, "end": v(-5.26, 6.25) * mm, "construction": true});
            skLineSegment(sketch, "E26.28", {"start": v(3.25, -2.49) * mm, "end": v(2.93, -0.73) * mm, "construction": true});
            skArc(sketch, "E26.29", {"start": v(6.25, -5.26) * mm, "mid": v(6.14, -4.71) * mm, "end": v(6.6, -4.4) * mm, "construction": true});
            skLineSegment(sketch, "E26.30", {"start": v(7.5, 3.9) * mm, "end": v(7.5, 2.1) * mm, "construction": true});
            skArc(sketch, "E26.31", {"start": v(1.35, 0) * mm, "mid": v(1.25, 0.52) * mm, "end": v(0.95, 0.95) * mm, "construction": true});
            skLineSegment(sketch, "E26.32", {"start": v(7.35, -6.36) * mm, "end": v(6.25, -5.26) * mm, "construction": true});
            skLineSegment(sketch, "E26.33", {"start": v(-6.36, -7.35) * mm, "end": v(-5.26, -6.25) * mm, "construction": true});
            skLineSegment(sketch, "E26.34", {"start": v(-7.35, -6.36) * mm, "end": v(-6.25, -5.26) * mm, "construction": true});
            skLineSegment(sketch, "E26.35", {"start": v(0, 0) * mm, "end": v(-7.5, -7.5) * mm, "construction": true});
            skLineSegment(sketch, "E26.36", {"start": v(-5.9, -2.9) * mm, "end": v(-3.74, -2.9) * mm, "construction": true});
            skArc(sketch, "E26.37", {"start": v(-5.26, -6.25) * mm, "mid": v(-4.71, -6.14) * mm, "end": v(-4.4, -6.6) * mm, "construction": true});
            skArc(sketch, "E26.38", {"start": v(-5.26, 6.25) * mm, "mid": v(-4.71, 6.14) * mm, "end": v(-4.4, 6.6) * mm, "construction": true});
            skLineSegment(sketch, "E26.39", {"start": v(2.49, 3.25) * mm, "end": v(0.73, 2.93) * mm, "construction": true});
            skLineSegment(sketch, "E26.40", {"start": v(7.35, 6.36) * mm, "end": v(6.25, 5.26) * mm, "construction": true});
            skLineSegment(sketch, "E26.41", {"start": v(2.9, -5.9) * mm, "end": v(2.9, -3.74) * mm, "construction": true});
            skLineSegment(sketch, "E26.42", {"start": v(-2.9, -5.9) * mm, "end": v(-2.9, -3.74) * mm, "construction": true});
            skLineSegment(sketch, "E26.43", {"start": v(3.9, -7.5) * mm, "end": v(2.1, -7.5) * mm, "construction": true});
            skArc(sketch, "E26.44", {"start": v(0, -1.35) * mm, "mid": v(0.52, -1.25) * mm, "end": v(0.95, -0.95) * mm, "construction": true});
            skArc(sketch, "E26.45", {"start": v(-6.25, 5.26) * mm, "mid": v(-6.14, 4.71) * mm, "end": v(-6.6, 4.4) * mm, "construction": true});
            skArc(sketch, "E26.46", {"start": v(-1.35, 0) * mm, "mid": v(-1.25, 0.52) * mm, "end": v(-0.95, 0.95) * mm, "construction": true});
            skLineSegment(sketch, "E26.47", {"start": v(-2.4, 0) * mm, "end": v(-1.35, 0) * mm, "construction": true});
            skLineSegment(sketch, "E26.48", {"start": v(0, -2.4) * mm, "end": v(0, -1.35) * mm, "construction": true});
            skLineSegment(sketch, "E26.49", {"start": v(0, 2.4) * mm, "end": v(0, 1.35) * mm, "construction": true});
            skArc(sketch, "E26.50", {"start": v(6.1, 2.1) * mm, "mid": v(6.25, 1.75) * mm, "end": v(6.6, 1.6) * mm, "construction": true});
            skLineSegment(sketch, "E26.51", {"start": v(6.6, -4.4) * mm, "end": v(7, -4.4) * mm, "construction": true});
            skLineSegment(sketch, "E26.52", {"start": v(-6.1, -2.1) * mm, "end": v(-6.1, -2.7) * mm, "construction": true});
            skArc(sketch, "E26.53", {"start": v(-7, -1.6) * mm, "mid": v(-7.35, -1.75) * mm, "end": v(-7.5, -2.1) * mm, "construction": true});
            skArc(sketch, "E26.54", {"start": v(-1.6, -7) * mm, "mid": v(-1.75, -7.35) * mm, "end": v(-2.1, -7.5) * mm, "construction": true});
            skLineSegment(sketch, "E26.55", {"start": v(7, -1.6) * mm, "end": v(6.6, -1.6) * mm, "construction": true});
            skArc(sketch, "E26.56", {"start": v(3.74, -2.9) * mm, "mid": v(3.42, -2.78) * mm, "end": v(3.25, -2.49) * mm, "construction": true});
            skArc(sketch, "E26.57", {"start": v(-3.74, 2.9) * mm, "mid": v(-3.42, 2.78) * mm, "end": v(-3.25, 2.49) * mm, "construction": true});
            skArc(sketch, "E26.58", {"start": v(1.6, -7) * mm, "mid": v(1.75, -7.35) * mm, "end": v(2.1, -7.5) * mm, "construction": true});
            skArc(sketch, "E26.59", {"start": v(1.6, 7) * mm, "mid": v(1.75, 7.35) * mm, "end": v(2.1, 7.5) * mm, "construction": true});
            skLineSegment(sketch, "E26.60", {"start": v(1.6, -7) * mm, "end": v(1.6, -6.6) * mm, "construction": true});
            skArc(sketch, "E26.61", {"start": v(-3.9, 7.5) * mm, "mid": v(-4.26, 7.35) * mm, "end": v(-4.4, 7) * mm, "construction": true});
            skArc(sketch, "E26.62", {"start": v(7, -1.6) * mm, "mid": v(7.35, -1.75) * mm, "end": v(7.5, -2.1) * mm, "construction": true});
            skArc(sketch, "E26.63", {"start": v(-6.1, 2.1) * mm, "mid": v(-6.25, 1.75) * mm, "end": v(-6.6, 1.6) * mm, "construction": true});
            skArc(sketch, "E26.64", {"start": v(-7.5, -3.9) * mm, "mid": v(-7.35, -4.26) * mm, "end": v(-7, -4.4) * mm, "construction": true});
            skArc(sketch, "E26.65", {"start": v(7.5, -3.9) * mm, "mid": v(7.35, -4.26) * mm, "end": v(7, -4.4) * mm, "construction": true});
            skArc(sketch, "E26.66", {"start": v(-3.9, -7.5) * mm, "mid": v(-4.26, -7.35) * mm, "end": v(-4.4, -7) * mm, "construction": true});
            skArc(sketch, "E26.67", {"start": v(-1.35, 0) * mm, "mid": v(-1.25, -0.52) * mm, "end": v(-0.95, -0.95) * mm, "construction": true});
            skLineSegment(sketch, "E26.68", {"start": v(-6.1, 2.1) * mm, "end": v(-6.1, 2.7) * mm, "construction": true});
            skArc(sketch, "E26.69", {"start": v(-3.74, -2.9) * mm, "mid": v(-3.42, -2.78) * mm, "end": v(-3.25, -2.49) * mm, "construction": true});
            skArc(sketch, "E26.70", {"start": v(1.35, 0) * mm, "mid": v(1.25, -0.52) * mm, "end": v(0.95, -0.95) * mm, "construction": true});
            skArc(sketch, "E26.71", {"start": v(-2.9, -3.74) * mm, "mid": v(-2.78, -3.42) * mm, "end": v(-2.49, -3.25) * mm, "construction": true});
            skArc(sketch, "E26.72", {"start": v(-6.1, -2.1) * mm, "mid": v(-6.25, -1.75) * mm, "end": v(-6.6, -1.6) * mm, "construction": true});
            skArc(sketch, "E26.73", {"start": v(2.1, -6.1) * mm, "mid": v(1.75, -6.25) * mm, "end": v(1.6, -6.6) * mm, "construction": true});
            skArc(sketch, "E26.74", {"start": v(7, 1.6) * mm, "mid": v(7.35, 1.75) * mm, "end": v(7.5, 2.1) * mm, "construction": true});
            skLineSegment(sketch, "E26.75", {"start": v(4.4, 6.6) * mm, "end": v(4.4, 7) * mm, "construction": true});
            skArc(sketch, "E26.76", {"start": v(-7.5, 3.9) * mm, "mid": v(-7.35, 4.26) * mm, "end": v(-7, 4.4) * mm, "construction": true});
            skArc(sketch, "E26.77", {"start": v(-2.9, 3.74) * mm, "mid": v(-2.78, 3.42) * mm, "end": v(-2.49, 3.25) * mm, "construction": true});
            skArc(sketch, "E26.78", {"start": v(3.9, -7.5) * mm, "mid": v(4.26, -7.35) * mm, "end": v(4.4, -7) * mm, "construction": true});
            skLineSegment(sketch, "E26.79", {"start": v(1.6, 7) * mm, "end": v(1.6, 6.6) * mm, "construction": true});
            skLineSegment(sketch, "E26.80", {"start": v(4.4, -6.6) * mm, "end": v(4.4, -7) * mm, "construction": true});
            skArc(sketch, "E26.81", {"start": v(-2.1, 6.1) * mm, "mid": v(-1.75, 6.25) * mm, "end": v(-1.6, 6.6) * mm, "construction": true});
            skArc(sketch, "E26.82", {"start": v(2.9, -3.74) * mm, "mid": v(2.78, -3.42) * mm, "end": v(2.49, -3.25) * mm, "construction": true});
            skLineSegment(sketch, "E26.83", {"start": v(-4.4, -6.6) * mm, "end": v(-4.4, -7) * mm, "construction": true});
            skArc(sketch, "E26.84", {"start": v(-1.6, 7) * mm, "mid": v(-1.75, 7.35) * mm, "end": v(-2.1, 7.5) * mm, "construction": true});
            skLineSegment(sketch, "E26.85", {"start": v(-6.6, -4.4) * mm, "end": v(-7, -4.4) * mm, "construction": true});
            skLineSegment(sketch, "E26.86", {"start": v(-4.4, 6.6) * mm, "end": v(-4.4, 7) * mm, "construction": true});
            skLineSegment(sketch, "E26.87", {"start": v(6.1, 2.1) * mm, "end": v(6.1, 2.7) * mm, "construction": true});
            skArc(sketch, "E26.88", {"start": v(7.5, 3.9) * mm, "mid": v(7.35, 4.26) * mm, "end": v(7, 4.4) * mm, "construction": true});
            skArc(sketch, "E26.89", {"start": v(2.9, 3.74) * mm, "mid": v(2.78, 3.42) * mm, "end": v(2.49, 3.25) * mm, "construction": true});
            skArc(sketch, "E26.90", {"start": v(3.9, 7.5) * mm, "mid": v(4.26, 7.35) * mm, "end": v(4.4, 7) * mm, "construction": true});
            skArc(sketch, "E26.91", {"start": v(3.74, 2.9) * mm, "mid": v(3.42, 2.78) * mm, "end": v(3.25, 2.49) * mm, "construction": true});
            skArc(sketch, "E26.92", {"start": v(6.1, -2.1) * mm, "mid": v(6.25, -1.75) * mm, "end": v(6.6, -1.6) * mm, "construction": true});
            skLineSegment(sketch, "E26.93", {"start": v(6.6, 4.4) * mm, "end": v(7, 4.4) * mm, "construction": true});
            skArc(sketch, "E26.94", {"start": v(-7, 1.6) * mm, "mid": v(-7.35, 1.75) * mm, "end": v(-7.5, 2.1) * mm, "construction": true});
            skLineSegment(sketch, "E26.95", {"start": v(6.1, -2.1) * mm, "end": v(6.1, -2.7) * mm, "construction": true});
            skArc(sketch, "E26.96", {"start": v(-6.36, -7.35) * mm, "mid": v(-6.53, -7.46) * mm, "end": v(-6.72, -7.5) * mm, "construction": true});
            skArc(sketch, "E26.97", {"start": v(7.35, 6.36) * mm, "mid": v(7.46, 6.53) * mm, "end": v(7.5, 6.72) * mm, "construction": true});
            skLineSegment(sketch, "E26.98", {"start": v(7, 7.5) * mm, "end": v(6.72, 7.5) * mm, "construction": true});
            skArc(sketch, "E26.99", {"start": v(-7.35, -6.36) * mm, "mid": v(-7.46, -6.53) * mm, "end": v(-7.5, -6.72) * mm, "construction": true});
            skLineSegment(sketch, "E26.100", {"start": v(7, 1.6) * mm, "end": v(6.6, 1.6) * mm, "construction": true});
            skArc(sketch, "E26.101", {"start": v(7.5, 7) * mm, "mid": v(7.35, 7.35) * mm, "end": v(7, 7.5) * mm, "construction": true});
            skArc(sketch, "E26.102", {"start": v(2.1, 6.1) * mm, "mid": v(1.75, 6.25) * mm, "end": v(1.6, 6.6) * mm, "construction": true});
            skArc(sketch, "E26.103", {"start": v(0.57, -2.6) * mm, "mid": v(0.51, -2.46) * mm, "end": v(0.37, -2.4) * mm, "construction": true});
            skLineSegment(sketch, "E26.104", {"start": v(2.1, -6.1) * mm, "end": v(2.7, -6.1) * mm, "construction": true});
            skLineSegment(sketch, "E26.105", {"start": v(2.1, 6.1) * mm, "end": v(2.7, 6.1) * mm, "construction": true});
            skLineSegment(sketch, "E26.106", {"start": v(-7, 7.5) * mm, "end": v(-6.72, 7.5) * mm, "construction": true});
            skLineSegment(sketch, "E26.107", {"start": v(0.57, 2.73) * mm, "end": v(0.57, 2.6) * mm, "construction": true});
            skLineSegment(sketch, "E26.108", {"start": v(-7, -1.6) * mm, "end": v(-6.6, -1.6) * mm, "construction": true});
            skLineSegment(sketch, "E26.109", {"start": v(-2.1, 6.1) * mm, "end": v(-2.7, 6.1) * mm, "construction": true});
            skArc(sketch, "E26.110", {"start": v(-2.7, 6.1) * mm, "mid": v(-2.84, 6.04) * mm, "end": v(-2.9, 5.9) * mm, "construction": true});
            skLineSegment(sketch, "E26.111", {"start": v(-7.5, -7) * mm, "end": v(-7.5, -6.72) * mm, "construction": true});
            skArc(sketch, "E26.112", {"start": v(-7.5, -7) * mm, "mid": v(-7.35, -7.35) * mm, "end": v(-7, -7.5) * mm, "construction": true});
            skLineSegment(sketch, "E26.113", {"start": v(-6.6, 4.4) * mm, "end": v(-7, 4.4) * mm, "construction": true});
            skArc(sketch, "E26.114", {"start": v(6.36, 7.35) * mm, "mid": v(6.53, 7.46) * mm, "end": v(6.72, 7.5) * mm, "construction": true});
            skArc(sketch, "E26.115", {"start": v(-6.36, 7.35) * mm, "mid": v(-6.53, 7.46) * mm, "end": v(-6.72, 7.5) * mm, "construction": true});
            skArc(sketch, "E26.116", {"start": v(-2.1, -6.1) * mm, "mid": v(-1.75, -6.25) * mm, "end": v(-1.6, -6.6) * mm, "construction": true});
            skArc(sketch, "E26.117", {"start": v(0.57, -2.73) * mm, "mid": v(0.62, -2.86) * mm, "end": v(0.73, -2.93) * mm, "construction": true});
            skArc(sketch, "E26.118", {"start": v(6.1, -2.7) * mm, "mid": v(6.04, -2.84) * mm, "end": v(5.9, -2.9) * mm, "construction": true});
            skArc(sketch, "E26.119", {"start": v(0.57, 2.73) * mm, "mid": v(0.62, 2.86) * mm, "end": v(0.73, 2.93) * mm, "construction": true});
            skArc(sketch, "E26.120", {"start": v(0.57, 2.6) * mm, "mid": v(0.51, 2.46) * mm, "end": v(0.37, 2.4) * mm, "construction": true});
            skArc(sketch, "E26.121", {"start": v(6.1, 2.7) * mm, "mid": v(6.04, 2.84) * mm, "end": v(5.9, 2.9) * mm, "construction": true});
            skLineSegment(sketch, "E26.122", {"start": v(-7, 1.6) * mm, "end": v(-6.6, 1.6) * mm, "construction": true});
            skArc(sketch, "E26.123", {"start": v(-7.5, 7) * mm, "mid": v(-7.35, 7.35) * mm, "end": v(-7, 7.5) * mm, "construction": true});
            skArc(sketch, "E26.124", {"start": v(-2.7, -6.1) * mm, "mid": v(-2.84, -6.04) * mm, "end": v(-2.9, -5.9) * mm, "construction": true});
            skLineSegment(sketch, "E26.125", {"start": v(-2.1, -6.1) * mm, "end": v(-2.7, -6.1) * mm, "construction": true});
            skLineSegment(sketch, "E26.126", {"start": v(-1.6, 7) * mm, "end": v(-1.6, 6.6) * mm, "construction": true});
            skArc(sketch, "E26.127", {"start": v(-6.1, -2.7) * mm, "mid": v(-6.04, -2.84) * mm, "end": v(-5.9, -2.9) * mm, "construction": true});
            skLineSegment(sketch, "E26.128", {"start": v(-1.6, -7) * mm, "end": v(-1.6, -6.6) * mm, "construction": true});
            skArc(sketch, "E26.129", {"start": v(2.7, -6.1) * mm, "mid": v(2.84, -6.04) * mm, "end": v(2.9, -5.9) * mm, "construction": true});
            skLineSegment(sketch, "E26.130", {"start": v(2.4, -0.37) * mm, "end": v(2.4, 0) * mm, "construction": true});
            skArc(sketch, "E26.131", {"start": v(7.5, -7) * mm, "mid": v(7.35, -7.35) * mm, "end": v(7, -7.5) * mm, "construction": true});
            skArc(sketch, "E26.132", {"start": v(2.7, 6.1) * mm, "mid": v(2.84, 6.04) * mm, "end": v(2.9, 5.9) * mm, "construction": true});
            skArc(sketch, "E26.133", {"start": v(-6.1, 2.7) * mm, "mid": v(-6.04, 2.84) * mm, "end": v(-5.9, 2.9) * mm, "construction": true});
            skArc(sketch, "E26.134", {"start": v(7.35, -6.36) * mm, "mid": v(7.46, -6.53) * mm, "end": v(7.5, -6.72) * mm, "construction": true});
            skLineSegment(sketch, "E26.135", {"start": v(-7.5, 7) * mm, "end": v(-7.5, 6.72) * mm, "construction": true});
            skLineSegment(sketch, "E26.136", {"start": v(0.37, 2.4) * mm, "end": v(0, 2.4) * mm, "construction": true});
            skArc(sketch, "E26.137", {"start": v(-0.57, 2.73) * mm, "mid": v(-0.62, 2.86) * mm, "end": v(-0.73, 2.93) * mm, "construction": true});
            skArc(sketch, "E26.138", {"start": v(-0.57, -2.6) * mm, "mid": v(-0.51, -2.46) * mm, "end": v(-0.37, -2.4) * mm, "construction": true});
            skLineSegment(sketch, "E26.139", {"start": v(-2.4, -0.37) * mm, "end": v(-2.4, 0) * mm, "construction": true});
            skLineSegment(sketch, "E26.140", {"start": v(7.5, 7) * mm, "end": v(7.5, 6.72) * mm, "construction": true});
            skLineSegment(sketch, "E26.141", {"start": v(-7, -7.5) * mm, "end": v(-6.72, -7.5) * mm, "construction": true});
            skLineSegment(sketch, "E26.142", {"start": v(2.4, 0.37) * mm, "end": v(2.4, 0) * mm, "construction": true});
            skLineSegment(sketch, "E26.143", {"start": v(7.5, -7) * mm, "end": v(7.5, -6.72) * mm, "construction": true});
            skArc(sketch, "E26.144", {"start": v(-7.35, 6.36) * mm, "mid": v(-7.46, 6.53) * mm, "end": v(-7.5, 6.72) * mm, "construction": true});
            skLineSegment(sketch, "E26.145", {"start": v(0.37, -2.4) * mm, "end": v(0, -2.4) * mm, "construction": true});
            skLineSegment(sketch, "E26.146", {"start": v(7, -7.5) * mm, "end": v(6.72, -7.5) * mm, "construction": true});
            skArc(sketch, "E26.147", {"start": v(-0.57, 2.6) * mm, "mid": v(-0.51, 2.46) * mm, "end": v(-0.37, 2.4) * mm, "construction": true});
            skLineSegment(sketch, "E26.148", {"start": v(0.57, -2.73) * mm, "end": v(0.57, -2.6) * mm, "construction": true});
            skArc(sketch, "E26.149", {"start": v(6.36, -7.35) * mm, "mid": v(6.53, -7.46) * mm, "end": v(6.72, -7.5) * mm, "construction": true});
            skArc(sketch, "E26.150", {"start": v(-0.57, -2.73) * mm, "mid": v(-0.62, -2.86) * mm, "end": v(-0.73, -2.93) * mm, "construction": true});
            skLineSegment(sketch, "E26.151", {"start": v(-0.37, -2.4) * mm, "end": v(0, -2.4) * mm, "construction": true});
            skLineSegment(sketch, "E26.152", {"start": v(-0.37, 2.4) * mm, "end": v(0, 2.4) * mm, "construction": true});
            skArc(sketch, "E26.153", {"start": v(2.73, -0.57) * mm, "mid": v(2.86, -0.62) * mm, "end": v(2.93, -0.73) * mm, "construction": true});
            skArc(sketch, "E26.154", {"start": v(2.73, 0.57) * mm, "mid": v(2.86, 0.62) * mm, "end": v(2.93, 0.73) * mm, "construction": true});
            skArc(sketch, "E26.155", {"start": v(-2.73, 0.57) * mm, "mid": v(-2.86, 0.62) * mm, "end": v(-2.93, 0.73) * mm, "construction": true});
            skLineSegment(sketch, "E26.156", {"start": v(-2.4, 0.37) * mm, "end": v(-2.4, 0) * mm, "construction": true});
            skLineSegment(sketch, "E26.157", {"start": v(-0.57, 2.73) * mm, "end": v(-0.57, 2.6) * mm, "construction": true});
            skArc(sketch, "E26.158", {"start": v(-2.6, -0.57) * mm, "mid": v(-2.46, -0.51) * mm, "end": v(-2.4, -0.37) * mm, "construction": true});
            skLineSegment(sketch, "E26.159", {"start": v(2.73, 0.57) * mm, "end": v(2.6, 0.57) * mm, "construction": true});
            skArc(sketch, "E26.160", {"start": v(-2.6, 0.57) * mm, "mid": v(-2.46, 0.51) * mm, "end": v(-2.4, 0.37) * mm, "construction": true});
            skLineSegment(sketch, "E26.161", {"start": v(-2.73, -0.57) * mm, "end": v(-2.6, -0.57) * mm, "construction": true});
            skLineSegment(sketch, "E26.162", {"start": v(-0.57, -2.73) * mm, "end": v(-0.57, -2.6) * mm, "construction": true});
            skArc(sketch, "E26.163", {"start": v(2.6, -0.57) * mm, "mid": v(2.46, -0.51) * mm, "end": v(2.4, -0.37) * mm, "construction": true});
            skArc(sketch, "E26.164", {"start": v(2.6, 0.57) * mm, "mid": v(2.46, 0.51) * mm, "end": v(2.4, 0.37) * mm, "construction": true});
            skArc(sketch, "E26.165", {"start": v(-2.73, -0.57) * mm, "mid": v(-2.86, -0.62) * mm, "end": v(-2.93, -0.73) * mm, "construction": true});
            skLineSegment(sketch, "E26.166", {"start": v(-2.73, 0.57) * mm, "end": v(-2.6, 0.57) * mm, "construction": true});
            skLineSegment(sketch, "E26.167", {"start": v(2.73, -0.57) * mm, "end": v(2.6, -0.57) * mm, "construction": true});
            skCircle(sketch, "E27", {"center": v(0, 10.02) * mm, "radius": 3.18 * mm, "construction": true});
            skCircle(sketch, "E28", {"center": v(-10.02, 0) * mm, "radius": 3.18 * mm, "construction": true});
            skCircle(sketch, "E29", {"center": v(10.02, 0) * mm, "radius": 3.18 * mm, "construction": true});
            skLineSegment(sketch, "E30.bottom", {"start": v(8.25, 8) * mm, "end": v(-8.25, 8) * mm, "construction": true});
            skLineSegment(sketch, "E30.top", {"start": v(8.25, -8) * mm, "end": v(-8.25, -8) * mm, "construction": true});
            skLineSegment(sketch, "E30.left", {"start": v(8.25, 8) * mm, "end": v(8.25, -8) * mm, "construction": true});
            skLineSegment(sketch, "E30.right", {"start": v(-8.25, 8) * mm, "end": v(-8.25, -8) * mm, "construction": true});
            skLineSegment(sketch, "E31", {"start": v(0, 14.2) * mm, "end": v(-15, 14.2) * mm, "construction": true});
            skLineSegment(sketch, "E32", {"start": v(-15, 14.2) * mm, "end": v(-15, -13) * mm, "construction": true});
            skLineSegment(sketch, "E33.MirrorCS", {"start": v(0, 14.2) * mm, "end": v(15, 14.2) * mm, "construction": true});
            skLineSegment(sketch, "E34.MirrorCS", {"start": v(15, 14.2) * mm, "end": v(15, -13) * mm, "construction": true});
            skLineSegment(sketch, "E35", {"start": v(-15, -13) * mm, "end": v(-8.25, -13) * mm, "construction": true});
            skLineSegment(sketch, "E36", {"start": v(-8.25, -8) * mm, "end": v(-8.25, -13) * mm, "construction": true});
            skLineSegment(sketch, "E37.MirrorCS", {"start": v(8.25, -8) * mm, "end": v(8.25, -13) * mm, "construction": true});
            skLineSegment(sketch, "E38.MirrorCS", {"start": v(15, -13) * mm, "end": v(8.25, -13) * mm, "construction": true});
            skLineSegment(sketch, "E39", {"start": v(-3.18, 10.02) * mm, "end": v(-3.18, 8) * mm, "construction": true});
            skLineSegment(sketch, "E40", {"start": v(-15, 12.2) * mm, "end": v(-9, 12.2) * mm, "construction": true});
            skLineSegment(sketch, "E41", {"start": v(-9, 12.2) * mm, "end": v(-9, 9.4) * mm, "construction": true});
            skLineSegment(sketch, "E42", {"start": v(-9, 9.4) * mm, "end": v(-15, 9.4) * mm, "construction": true});
            skLineSegment(sketch, "E43.MirrorCS", {"start": v(15, 12.2) * mm, "end": v(9, 12.2) * mm, "construction": true});
            skLineSegment(sketch, "E44.MirrorCS", {"start": v(9, 12.2) * mm, "end": v(9, 9.4) * mm, "construction": true});
            skLineSegment(sketch, "E45.MirrorCS", {"start": v(9, 9.4) * mm, "end": v(15, 9.4) * mm, "construction": true});
            skLineSegment(sketch, "E46", {"start": v(-12, 12.2) * mm, "end": v(-12, 14.2) * mm, "construction": true});
            skLineSegment(sketch, "E47.MirrorCS", {"start": v(12, 12.2) * mm, "end": v(12, 14.2) * mm, "construction": true});
            skSolve(sketch);
        }
        {
            var Q0;
            Q0=qCreatedBy(makeId("Top.planeOp"),FACE);
            var sketch = newSketch(context, id + "F2", { "sketchPlane" : qUnion([Q0])});
            skLineSegment(sketch, "E48.0", {"start": v(-15, 14.2) * mm, "end": v(-15, -13) * mm});
            skLineSegment(sketch, "E49.0", {"start": v(0, 14.2) * mm, "end": v(-15, 14.2) * mm});
            skLineSegment(sketch, "E50.0", {"start": v(15, 14.2) * mm, "end": v(15, -13) * mm});
            skLineSegment(sketch, "E51.0", {"start": v(0, 14.2) * mm, "end": v(15, 14.2) * mm});
            skLineSegment(sketch, "E52.0", {"start": v(15, -13) * mm, "end": v(8.25, -13) * mm});
            skLineSegment(sketch, "E53.0", {"start": v(8.25, -8) * mm, "end": v(8.25, -13) * mm});
            skLineSegment(sketch, "E54.0", {"start": v(-8.25, -8) * mm, "end": v(-8.25, -13) * mm});
            skLineSegment(sketch, "E55.0", {"start": v(-15, -13) * mm, "end": v(-8.25, -13) * mm});
            skPoint(sketch, "E56.0", {"position": v(-10.02, 0) * mm});
            skPoint(sketch, "E57.0", {"position": v(10.02, 0) * mm});
            skPoint(sketch, "E58.0", {"position": v(0, 10.02) * mm});
            skLineSegment(sketch, "E59.0", {"start": v(-8.25, 8) * mm, "end": v(-8.25, -8) * mm});
            skLineSegment(sketch, "E60.0", {"start": v(8.25, 8) * mm, "end": v(-8.25, 8) * mm});
            skLineSegment(sketch, "E61.0", {"start": v(8.25, 8) * mm, "end": v(8.25, -8) * mm});
            skLineSegment(sketch, "E62", {"start": v(-8.25, -10.5) * mm, "end": v(-15, -10.5) * mm, "construction": true});
            skLineSegment(sketch, "E63", {"start": v(-15, -9.4) * mm, "end": v(-12.8, -9.4) * mm});
            skLineSegment(sketch, "E64", {"start": v(-12.8, -9.4) * mm, "end": v(-12.8, -11.6) * mm});
            skLineSegment(sketch, "E65", {"start": v(-12.8, -11.6) * mm, "end": v(-15, -11.6) * mm});
            skLineSegment(sketch, "E66.MirrorCS", {"start": v(15, -9.4) * mm, "end": v(12.8, -9.4) * mm});
            skLineSegment(sketch, "E67.MirrorCS", {"start": v(12.8, -11.6) * mm, "end": v(15, -11.6) * mm});
            skLineSegment(sketch, "E68.MirrorCS", {"start": v(12.8, -9.4) * mm, "end": v(12.8, -11.6) * mm});
            skSolve(sketch);
        }
        {
            var Q0;
            Q0=qCreatedBy(makeId("Top.planeOp"),FACE);
            var sketch = newSketch(context, id + "F3", { "sketchPlane" : qUnion([Q0])});
            skCircle(sketch, "E69.0", {"center": v(-10.02, 0) * mm, "radius": 3.18 * mm, "construction": true});
            skCircle(sketch, "E70.0", {"center": v(-10.02, 0) * mm, "radius": 3.28 * mm, "construction": true});
            skLineSegment(sketch, "E71", {"start": v(-13.13, 1) * mm, "end": v(-21.48, 1) * mm});
            skLineSegment(sketch, "E72.0", {"start": v(-8.25, 8) * mm, "end": v(-8.25, -8) * mm, "construction": true});
            skLineSegment(sketch, "E73", {"start": v(-10.02, 3.28) * mm, "end": v(-8.25, 3.28) * mm});
            skArc(sketch, "E74", {"start": v(-13.13, 1) * mm, "mid": v(-11.95, 2.65) * mm, "end": v(-10.02, 3.28) * mm});
            skLineSegment(sketch, "E75", {"start": v(-8.25, 3.27) * mm, "end": v(-8.25, 0) * mm});
            skLineSegment(sketch, "E76.MirrorCS", {"start": v(-8.25, -3.27) * mm, "end": v(-8.25, 0) * mm});
            skLineSegment(sketch, "E77.MirrorCS", {"start": v(-10.02, -3.28) * mm, "end": v(-8.25, -3.28) * mm});
            skArc(sketch, "E78.MirrorCS", {"start": v(-13.13, -1) * mm, "mid": v(-11.95, -2.65) * mm, "end": v(-10.02, -3.28) * mm});
            skLineSegment(sketch, "E79.MirrorCS", {"start": v(-13.13, -1) * mm, "end": v(-21.48, -1) * mm});
            skLineSegment(sketch, "E80", {"start": v(-21.48, 1) * mm, "end": v(-21.48, -1) * mm});
            skLineSegment(sketch, "E81.1.0", {"start": v(-3.28, 10.02) * mm, "end": v(-3.28, 8.25) * mm});
            skLineSegment(sketch, "E81.1.1", {"start": v(-3.27, 8.25) * mm, "end": v(0, 8.25) * mm});
            skLineSegment(sketch, "E81.1.2", {"start": v(3.27, 8.25) * mm, "end": v(0, 8.25) * mm});
            skLineSegment(sketch, "E81.1.3", {"start": v(3.28, 10.02) * mm, "end": v(3.28, 8.25) * mm});
            skArc(sketch, "E81.1.4", {"start": v(1, 13.13) * mm, "mid": v(2.65, 11.95) * mm, "end": v(3.28, 10.02) * mm});
            skArc(sketch, "E81.1.5", {"start": v(-1, 13.13) * mm, "mid": v(-2.65, 11.95) * mm, "end": v(-3.28, 10.02) * mm});
            skLineSegment(sketch, "E81.1.6", {"start": v(-1, 13.13) * mm, "end": v(-1, 21.48) * mm});
            skLineSegment(sketch, "E81.1.7", {"start": v(1, 21.48) * mm, "end": v(-1, 21.48) * mm});
            skLineSegment(sketch, "E81.1.8", {"start": v(1, 13.13) * mm, "end": v(1, 21.48) * mm});
            skLineSegment(sketch, "E81.2.0", {"start": v(10.02, 3.28) * mm, "end": v(8.25, 3.28) * mm});
            skLineSegment(sketch, "E81.2.1", {"start": v(8.25, 3.27) * mm, "end": v(8.25, 0) * mm});
            skLineSegment(sketch, "E81.2.2", {"start": v(8.25, -3.27) * mm, "end": v(8.25, 0) * mm});
            skLineSegment(sketch, "E81.2.3", {"start": v(10.02, -3.28) * mm, "end": v(8.25, -3.28) * mm});
            skArc(sketch, "E81.2.4", {"start": v(13.13, -1) * mm, "mid": v(11.95, -2.65) * mm, "end": v(10.02, -3.28) * mm});
            skArc(sketch, "E81.2.5", {"start": v(13.13, 1) * mm, "mid": v(11.95, 2.65) * mm, "end": v(10.02, 3.28) * mm});
            skLineSegment(sketch, "E81.2.6", {"start": v(13.13, 1) * mm, "end": v(21.48, 1) * mm});
            skLineSegment(sketch, "E81.2.7", {"start": v(21.48, -1) * mm, "end": v(21.48, 1) * mm});
            skLineSegment(sketch, "E81.2.8", {"start": v(13.13, -1) * mm, "end": v(21.48, -1) * mm});
            skPoint(sketch, "E81.center", {"position": v(0, 0) * mm});
            skLineSegment(sketch, "E81.anchor1", {"start": v(0, 0) * mm, "end": v(-10.02, -3.28) * mm, "construction": true});
            skLineSegment(sketch, "E81.anchor2", {"start": v(0, 0) * mm, "end": v(10.02, 3.28) * mm, "construction": true});
            skLineSegment(sketch, "E82", {"start": v(-3.27, 8.25) * mm, "end": v(-3.27, 2.37) * mm});
            skLineSegment(sketch, "E83", {"start": v(3.27, 8.25) * mm, "end": v(3.27, 2.37) * mm});
            skLineSegment(sketch, "E84", {"start": v(3.27, 2.37) * mm, "end": v(3.27, 2.37) * mm});
            skLineSegment(sketch, "E85", {"start": v(3.27, 2.37) * mm, "end": v(-3.27, 2.37) * mm});
            skSolve(sketch);
        }
        {
            var Q0;
            Q0=qCreatedBy(makeId("Top.planeOp"),FACE);
            var sketch = newSketch(context, id + "F4", { "sketchPlane" : qUnion([Q0])});
            skLineSegment(sketch, "E86.0", {"start": v(-15, 12.2) * mm, "end": v(-9, 12.2) * mm});
            skLineSegment(sketch, "E87.0", {"start": v(-9, 9.4) * mm, "end": v(-15, 9.4) * mm});
            skLineSegment(sketch, "E88.0", {"start": v(-9, 12.2) * mm, "end": v(-9, 9.4) * mm});
            skLineSegment(sketch, "E89.0", {"start": v(9, 12.2) * mm, "end": v(9, 9.4) * mm});
            skLineSegment(sketch, "E90.0", {"start": v(15, 12.2) * mm, "end": v(9, 12.2) * mm});
            skLineSegment(sketch, "E91.0", {"start": v(9, 9.4) * mm, "end": v(15, 9.4) * mm});
            skLineSegment(sketch, "E92", {"start": v(-15, 12.2) * mm, "end": v(-15, 9.4) * mm});
            skLineSegment(sketch, "E93", {"start": v(15, 12.2) * mm, "end": v(15, 9.4) * mm});
            skSolve(sketch);
        }
        {
            var Q0;
            Q0=qCreatedBy(makeId("Top.planeOp"),FACE);
            var sketch = newSketch(context, id + "F5", { "sketchPlane" : qUnion([Q0])});
            skLineSegment(sketch, "E94.0", {"start": v(-12, 12.2) * mm, "end": v(-12, 14.2) * mm});
            skLineSegment(sketch, "E95.0", {"start": v(12, 12.2) * mm, "end": v(12, 14.2) * mm});
            skLineSegment(sketch, "E96", {"start": v(-12, 14.2) * mm, "end": v(-13.6, 14.2) * mm});
            skLineSegment(sketch, "E97", {"start": v(-13.6, 14.2) * mm, "end": v(-13.6, 12.2) * mm});
            skLineSegment(sketch, "E98", {"start": v(-13.6, 12.2) * mm, "end": v(-12, 12.2) * mm, "construction": true});
            skLineSegment(sketch, "E99.MirrorCS", {"start": v(12, 14.2) * mm, "end": v(13.6, 14.2) * mm});
            skLineSegment(sketch, "E100.MirrorCS", {"start": v(13.6, 14.2) * mm, "end": v(13.6, 12.2) * mm});
            skLineSegment(sketch, "E101.MirrorCS", {"start": v(13.6, 12.2) * mm, "end": v(12, 12.2) * mm, "construction": true});
            skLineSegment(sketch, "E102", {"start": v(12, 12.2) * mm, "end": v(12, 7.9) * mm});
            skLineSegment(sketch, "E103", {"start": v(12, 7.9) * mm, "end": v(13.6, 7.9) * mm});
            skLineSegment(sketch, "E104", {"start": v(13.6, 7.9) * mm, "end": v(13.6, 12.2) * mm});
            skLineSegment(sketch, "E105.MirrorCS", {"start": v(-13.6, 7.9) * mm, "end": v(-13.6, 12.2) * mm});
            skLineSegment(sketch, "E106.MirrorCS", {"start": v(-12, 7.9) * mm, "end": v(-13.6, 7.9) * mm});
            skLineSegment(sketch, "E107.MirrorCS", {"start": v(-12, 12.2) * mm, "end": v(-12, 7.9) * mm});
            skSolve(sketch);
        }
        {
            var Q0;
            Q0=makeQuery(id+"F2.imprint","IMPRINT",FACE,{"disambiguationData":[TD([[makeQuery(id+"F2.imprint","IMPRINT",EDGE,{"derivedFrom":sQuery(id+"F2.wireOp",EDGE,"E48.0")}),1.0]])]});
            extrude(context, id + "F6", {"entities" : qUnion([Q0]), "endBound" : BoundingType.SYMMETRIC, "depth" : 12 * mm});
        }
        {
            var Q0;
            Q0=makeQuery(id+"F0.imprint","IMPRINT",FACE,{"disambiguationData":[TD([[makeQuery(id+"F0.imprint","IMPRINT",EDGE,{"derivedFrom":sQuery(id+"F0.wireOp",EDGE,"E1")}),-1.0]])]});
            extrude(context, id + "F7", {"entities" : qUnion([Q0]), "endBound" : BoundingType.SYMMETRIC, "depth" : 320 * mm});
        }
        {
            var Q0;
            Q0 = qSketchRegion(id + "F4", true);
            extrude(context, id + "F8", {"entities" : qUnion([Q0]), "operationType" : NewBodyOperationType.REMOVE, "endBound" : BoundingType.SYMMETRIC, "depth" : 5.8 * mm});
        }
        {
            var Q0;
            Q0=makeQuery(id+"F5.imprint","IMPRINT",FACE,{"disambiguationData":[TD([[makeQuery(id+"F5.imprint","IMPRINT",EDGE,{"derivedFrom":sQuery(id+"F5.wireOp",EDGE,"E94.0")}),1.0]])]});
            var Q1;
            Q1=sQuery(id+"F5.wireOp",EDGE,"E94.0");
            revolve(context, id + "F9", {"operationType" : NewBodyOperationType.REMOVE, "entities" : qUnion([Q0]), "axis" : qUnion([Q1]), "revolveType" : RevolveType.FULL, "oppositeDirection" : true});
        }
        {
            var Q0;
            Q0=makeQuery(id+"F5.imprint","IMPRINT",FACE,{"disambiguationData":[TD([[makeQuery(id+"F5.imprint","IMPRINT",EDGE,{"derivedFrom":sQuery(id+"F5.wireOp",EDGE,"E95.0")}),-1.0]])]});
            var Q1;
            Q1=sQuery(id+"F5.wireOp",EDGE,"E95.0");
            revolve(context, id + "F10", {"operationType" : NewBodyOperationType.REMOVE, "entities" : qUnion([Q0]), "axis" : qUnion([Q1]), "revolveType" : RevolveType.FULL, "oppositeDirection" : true});
        }
        {
            var Q0;
            Q0 = qSketchRegion(id + "F3", true);
            extrude(context, id + "F11", {"entities" : qUnion([Q0]), "operationType" : NewBodyOperationType.REMOVE, "endBound" : BoundingType.SYMMETRIC, "depth" : 8 * mm});
        }
        {
            var Q0;
            Q0=makeQuery(id+"F6.opExtrude","SWEPT_EDGE",EDGE,{"disambiguationData":[OSD([sQuery(id+"F2.wireOp",EDGE,"E59.0"),sQuery(id+"F2.wireOp",EDGE,"E60.0")])]});
            var Q1;
            Q1=makeQuery(id+"F6.opExtrude","SWEPT_EDGE",EDGE,{"disambiguationData":[OSD([sQuery(id+"F2.wireOp",EDGE,"E60.0"),sQuery(id+"F2.wireOp",EDGE,"E61.0")])]});
            fillet(context, id + "F12", {"entities" : qUnion([Q0, Q1]), "radius" : 1 * mm, "allowEdgeOverflow" : false});
        }
        {
            var Q0;
            Q0=makeQuery(id+"F6.opExtrude","CAP_EDGE",EDGE,{"disambiguationData":[OSD([sQuery(id+"F2.wireOp",EDGE,"E68.MirrorCS")])],"isStart":true});
            var Q1;
            Q1=makeQuery(id+"F6.opExtrude","CAP_EDGE",EDGE,{"disambiguationData":[OSD([sQuery(id+"F2.wireOp",EDGE,"E64")])],"isStart":true});
            var Q2;
            Q2=makeQuery(id+"F6.opExtrude","CAP_EDGE",EDGE,{"disambiguationData":[OSD([sQuery(id+"F2.wireOp",EDGE,"E68.MirrorCS")])],"isStart":false});
            var Q3;
            Q3=makeQuery(id+"F6.opExtrude","CAP_EDGE",EDGE,{"disambiguationData":[OSD([sQuery(id+"F2.wireOp",EDGE,"E64")])],"isStart":false});
            fillet(context, id + "F16", {"entities" : qUnion([Q0, Q1, Q2, Q3]), "radius" : 1.5 * mm, "tangentPropagation" : true, "allowEdgeOverflow" : false});
        }
        {
            var Q0;
            Q0=makeQuery(id+"F6.opExtrude","CAP_FACE",FACE,{"disambiguationData":[OSD([sQuery(id+"F2.wireOp",EDGE,"E48.0"),sQuery(id+"F2.wireOp",EDGE,"E49.0"),sQuery(id+"F2.wireOp",EDGE,"E50.0"),sQuery(id+"F2.wireOp",EDGE,"E51.0"),sQuery(id+"F2.wireOp",EDGE,"E52.0"),sQuery(id+"F2.wireOp",EDGE,"E53.0"),sQuery(id+"F2.wireOp",EDGE,"E54.0"),sQuery(id+"F2.wireOp",EDGE,"E55.0"),sQuery(id+"F2.wireOp",EDGE,"E59.0"),sQuery(id+"F2.wireOp",EDGE,"E60.0"),sQuery(id+"F2.wireOp",EDGE,"E61.0"),sQuery(id+"F2.wireOp",EDGE,"E63"),sQuery(id+"F2.wireOp",EDGE,"E64"),sQuery(id+"F2.wireOp",EDGE,"E65"),sQuery(id+"F2.wireOp",EDGE,"E66.MirrorCS"),sQuery(id+"F2.wireOp",EDGE,"E67.MirrorCS"),sQuery(id+"F2.wireOp",EDGE,"E68.MirrorCS")])],"isStart":true});
            chamfer(context, id + "F13", {"entities" : qUnion([Q0]), "width" : 0.25 * mm});
        }
        {
            var Q0;
            Q0=makeQuery(id+"F6.opExtrude","CAP_FACE",FACE,{"disambiguationData":[OSD([sQuery(id+"F2.wireOp",EDGE,"E48.0"),sQuery(id+"F2.wireOp",EDGE,"E49.0"),sQuery(id+"F2.wireOp",EDGE,"E50.0"),sQuery(id+"F2.wireOp",EDGE,"E51.0"),sQuery(id+"F2.wireOp",EDGE,"E52.0"),sQuery(id+"F2.wireOp",EDGE,"E53.0"),sQuery(id+"F2.wireOp",EDGE,"E54.0"),sQuery(id+"F2.wireOp",EDGE,"E55.0"),sQuery(id+"F2.wireOp",EDGE,"E59.0"),sQuery(id+"F2.wireOp",EDGE,"E60.0"),sQuery(id+"F2.wireOp",EDGE,"E61.0"),sQuery(id+"F2.wireOp",EDGE,"E63"),sQuery(id+"F2.wireOp",EDGE,"E64"),sQuery(id+"F2.wireOp",EDGE,"E65"),sQuery(id+"F2.wireOp",EDGE,"E66.MirrorCS"),sQuery(id+"F2.wireOp",EDGE,"E67.MirrorCS"),sQuery(id+"F2.wireOp",EDGE,"E68.MirrorCS")])],"isStart":true});
            var sketch = newSketch(context, id + "F14", { "sketchPlane" : qUnion([Q0])});
            skLineSegment(sketch, "E108.0.1", {"start": v(8.25, 13) * mm, "end": v(15, 13) * mm});
            skLineSegment(sketch, "E108.0.3", {"start": v(15, 13) * mm, "end": v(8.25, 13) * mm});
            skCircle(sketch, "E109", {"center": v(15, 13) * mm, "radius": 1.25 * mm});
            skCircle(sketch, "E110.MirrorC", {"center": v(-15, 13) * mm, "radius": 1.25 * mm});
            skSolve(sketch);
        }
        {
            var Q0;
            Q0 = qSketchRegion(id + "F14", true);
            extrude(context, id + "F15", {"entities" : qUnion([Q0]), "operationType" : NewBodyOperationType.ADD, "oppositeDirection" : true, "depth" : 0.2 * mm});
        }
    });
